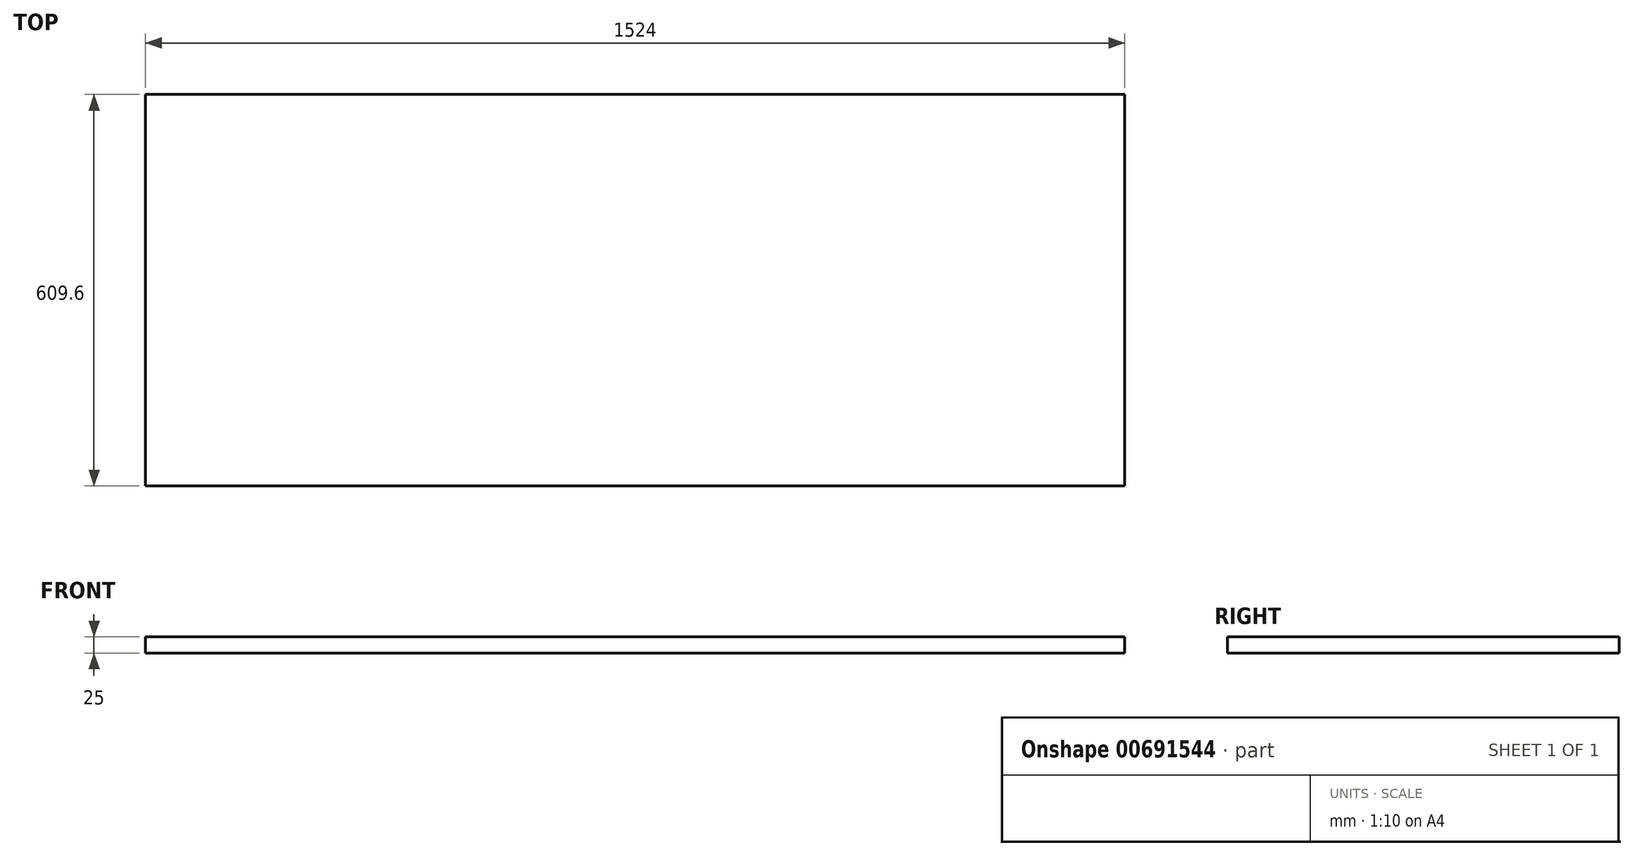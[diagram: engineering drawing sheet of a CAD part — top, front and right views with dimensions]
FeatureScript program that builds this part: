
annotation { "Feature Type Name" : "Feature", "Feature Type Description" : "" }
export const myFeature = defineFeature(function(context is Context, id is Id, definition is map)
    precondition{}
    {
        {
            var Q0;
            Q0=qCreatedBy(makeId("Top.planeOp"),FACE);
            var sketch = newSketch(context, id + "F0", { "sketchPlane" : qUnion([Q0])});
            skLineSegment(sketch, "E0.bottom", {"start": v(762, -304.8) * mm, "end": v(-762, -304.8) * mm});
            skLineSegment(sketch, "E0.top", {"start": v(762, 304.8) * mm, "end": v(-762, 304.8) * mm});
            skLineSegment(sketch, "E0.left", {"start": v(762, -304.8) * mm, "end": v(762, 304.8) * mm});
            skLineSegment(sketch, "E0.right", {"start": v(-762, -304.8) * mm, "end": v(-762, 304.8) * mm});
            skPoint(sketch, "E0.middle", {"position": v(0, 0) * mm});
            skSolve(sketch);
        }
        {
            var Q0;
            Q0 = qSketchRegion(id + "F0", true);
            extrude(context, id + "F1", {"entities" : qUnion([Q0]), "depth" : 25 * mm, "offsetDistance" : 25 * mm});
        }
    });
